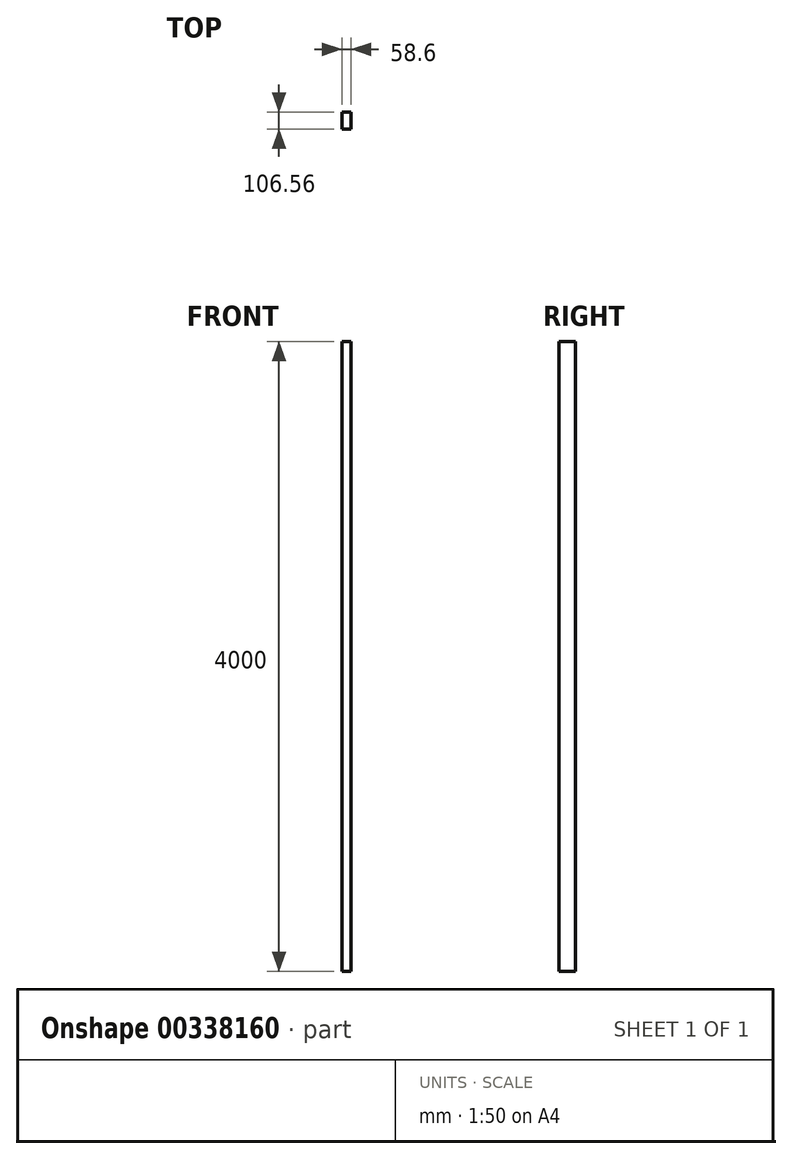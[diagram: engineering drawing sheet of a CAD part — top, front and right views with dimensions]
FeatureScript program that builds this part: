
annotation { "Feature Type Name" : "Feature", "Feature Type Description" : "" }
export const myFeature = defineFeature(function(context is Context, id is Id, definition is map)
    precondition{}
    {
        {
            var Q0;
            Q0=qCreatedBy(makeId("Top.planeOp"),FACE);
            var sketch = newSketch(context, id + "F0", { "sketchPlane" : qUnion([Q0])});
            skLineSegment(sketch, "E0.bottom", {"start": v(29.3, 53.28) * mm, "end": v(-29.3, 53.28) * mm});
            skLineSegment(sketch, "E0.top", {"start": v(29.3, -53.28) * mm, "end": v(-29.3, -53.28) * mm});
            skLineSegment(sketch, "E0.left", {"start": v(29.3, 53.28) * mm, "end": v(29.3, -53.28) * mm});
            skLineSegment(sketch, "E0.right", {"start": v(-29.3, 53.28) * mm, "end": v(-29.3, -53.28) * mm});
            skPoint(sketch, "E0.middle", {"position": v(0, 0) * mm});
            skSolve(sketch);
        }
        {
            var Q0;
            Q0=makeQuery(id+"F0.imprint","IMPRINT",FACE,{"disambiguationData":[TD([[makeQuery(id+"F0.imprint","IMPRINT",EDGE,{"derivedFrom":sQuery(id+"F0.wireOp",EDGE,"E0.bottom")}),1.0]])]});
            extrude(context, id + "F1", {"entities" : qUnion([Q0]), "depth" : 4000 * mm});
        }
    });
